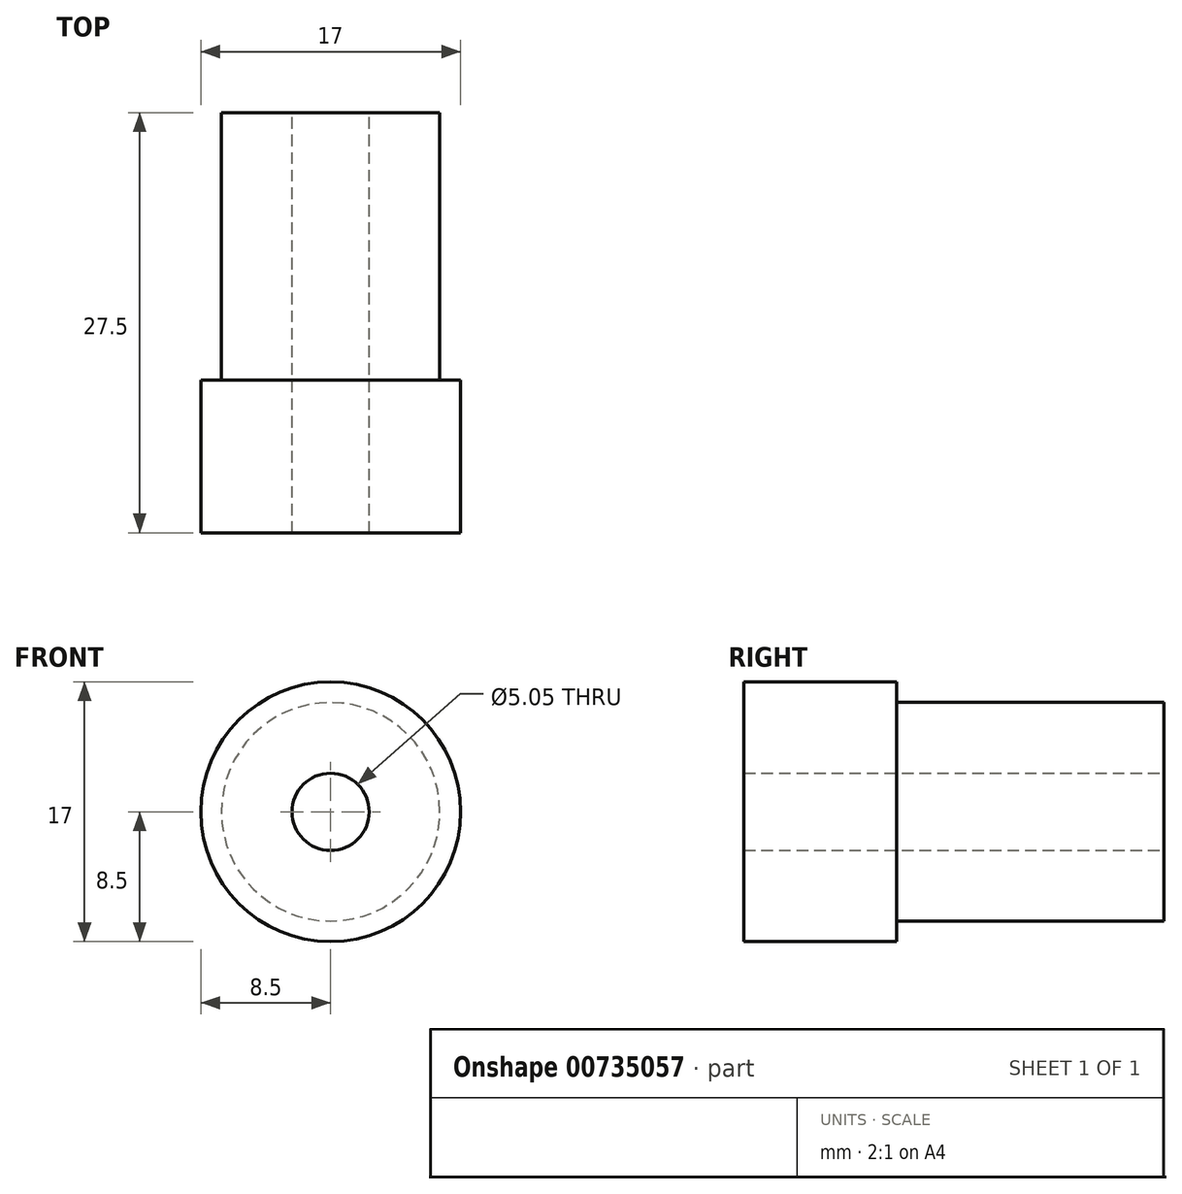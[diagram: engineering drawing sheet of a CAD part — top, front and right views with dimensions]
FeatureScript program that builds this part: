
annotation { "Feature Type Name" : "Feature", "Feature Type Description" : "" }
export const myFeature = defineFeature(function(context is Context, id is Id, definition is map)
    precondition{}
    {
        {
            var Q0;
            Q0=qCreatedBy(makeId("Front.planeOp"),FACE);
            var sketch = newSketch(context, id + "F0", { "sketchPlane" : qUnion([Q0])});
            skCircle(sketch, "E0", {"center": v(0, 0) * mm, "radius": 7.15 * mm});
            skCircle(sketch, "E1", {"center": v(0, 0) * mm, "radius": 2.52 * mm});
            skSolve(sketch);
        }
        {
            var Q0;
            Q0=qSketchRegion(id+"F0",true);
            extrude(context, id + "F1", {"entities" : qUnion([Q0]), "depth" : 17.5 * mm, "offsetDistance" : 25 * mm});
        }
        {
            var Q0;
            Q0=makeQuery(id+"F1.opExtrude","CAP_FACE",FACE,{"disambiguationData":[OSD([sQuery(id+"F0.wireOp",EDGE,"E0"),sQuery(id+"F0.wireOp",EDGE,"E1")])],"isStart":false});
            var sketch = newSketch(context, id + "F2", { "sketchPlane" : qUnion([Q0])});
            skCircle(sketch, "E2.0", {"center": v(0, 0) * mm, "radius": 2.52 * mm});
            skCircle(sketch, "E3", {"center": v(0, 0) * mm, "radius": 8.5 * mm});
            skSolve(sketch);
        }
        {
            var Q0;
            Q0=qSketchRegion(id+"F2",true);
            extrude(context, id + "F3", {"entities" : qUnion([Q0]), "operationType" : NewBodyOperationType.ADD, "depth" : 10 * mm, "offsetDistance" : 25 * mm});
        }
    });
